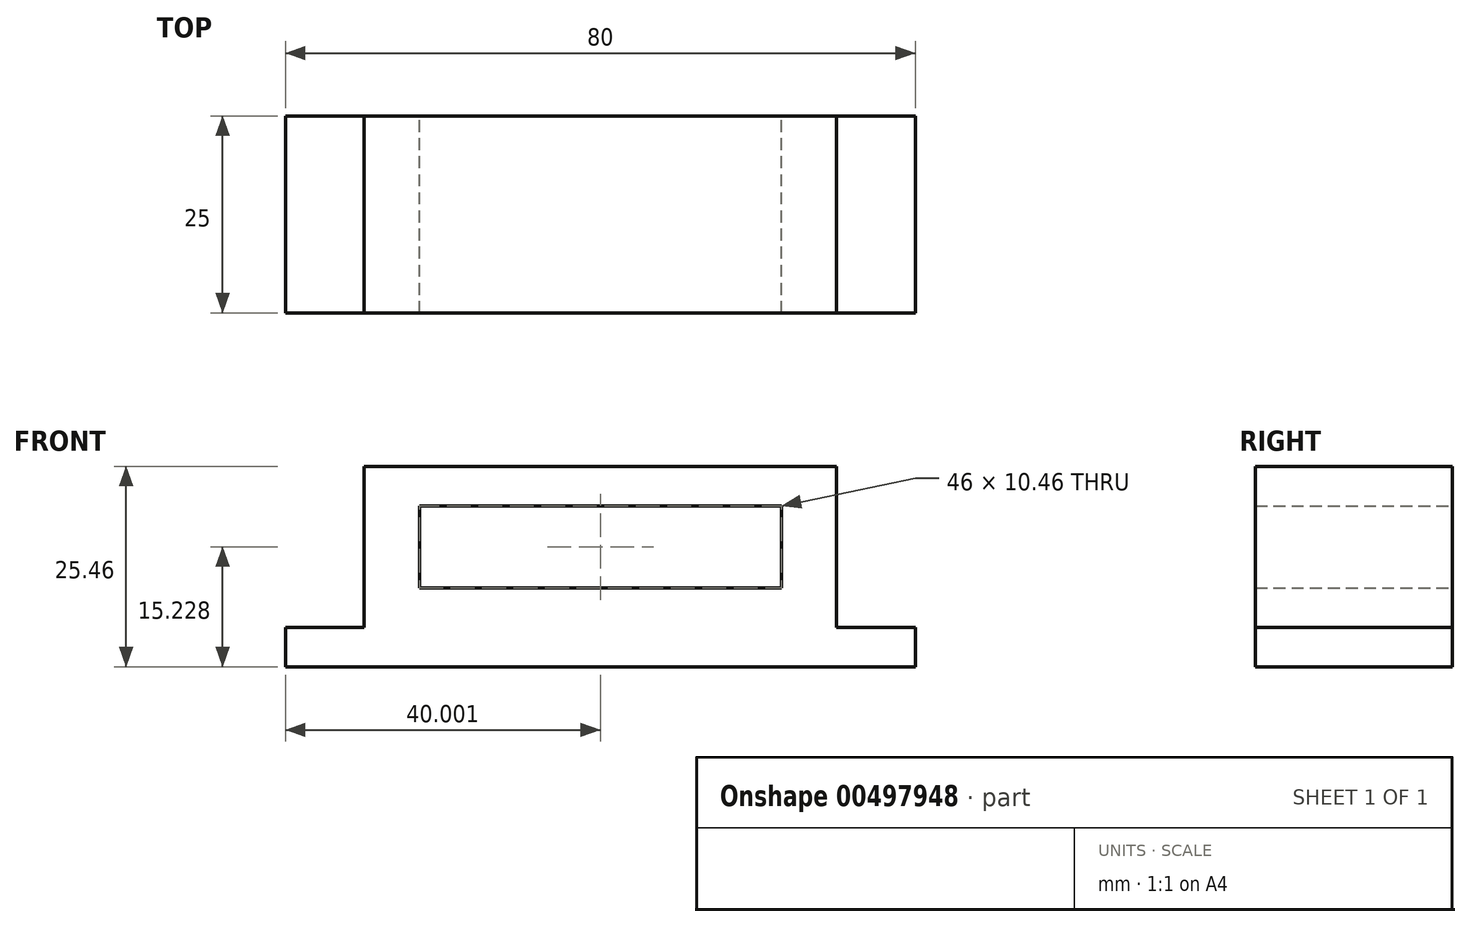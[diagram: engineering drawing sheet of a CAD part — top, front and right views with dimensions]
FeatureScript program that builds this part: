
annotation { "Feature Type Name" : "Feature", "Feature Type Description" : "" }
export const myFeature = defineFeature(function(context is Context, id is Id, definition is map)
    precondition{}
    {
        {
            var Q0;
            Q0=qCreatedBy(makeId("Front.planeOp"),FACE);
            var sketch = newSketch(context, id + "F0", { "sketchPlane" : qUnion([Q0])});
            skPoint(sketch, "E0.top.end.orphan", {"position": v(16.05, 5.84) * mm});
            skLineSegment(sketch, "E1.bottom", {"start": v(-31.65, 16.07) * mm, "end": v(28.35, 16.07) * mm});
            skLineSegment(sketch, "E1.top", {"start": v(-31.65, -4.4) * mm, "end": v(28.35, -4.4) * mm});
            skLineSegment(sketch, "E1.left", {"start": v(-31.65, 16.07) * mm, "end": v(-31.65, -4.4) * mm});
            skLineSegment(sketch, "E1.right", {"start": v(28.35, 16.07) * mm, "end": v(28.35, -4.4) * mm});
            skPoint(sketch, "E1.middle", {"position": v(-1.65, 5.84) * mm});
            skLineSegment(sketch, "E2.bottom", {"start": v(-24.65, 11.07) * mm, "end": v(21.35, 11.07) * mm});
            skLineSegment(sketch, "E2.top", {"start": v(-24.65, 0.6) * mm, "end": v(21.35, 0.6) * mm});
            skLineSegment(sketch, "E2.left", {"start": v(-24.65, 11.07) * mm, "end": v(-24.65, 0.6) * mm});
            skLineSegment(sketch, "E2.right", {"start": v(21.35, 11.07) * mm, "end": v(21.35, 0.6) * mm});
            skLineSegment(sketch, "E3.bottom", {"start": v(-41.65, -4.4) * mm, "end": v(38.35, -4.4) * mm});
            skLineSegment(sketch, "E3.top", {"start": v(-41.65, -9.4) * mm, "end": v(38.35, -9.4) * mm});
            skLineSegment(sketch, "E3.left", {"start": v(-41.65, -4.4) * mm, "end": v(-41.65, -9.4) * mm});
            skLineSegment(sketch, "E3.right", {"start": v(38.35, -4.4) * mm, "end": v(38.35, -9.4) * mm});
            skPoint(sketch, "E3.middle", {"position": v(-1.65, -6.9) * mm});
            skPoint(sketch, "E3.middle.positionSnap0", {"position": v(-1.65, -4.4) * mm});
            skPoint(sketch, "E3.centerSnap0", {"position": v(-1.65, -4.4) * mm});
            skSolve(sketch);
        }
        {
            var Q0;
            Q0 = qSketchRegion(id + "F0", true);
            extrude(context, id + "F1", {"entities" : qUnion([Q0]), "depth" : 25 * mm});
        }
    });
